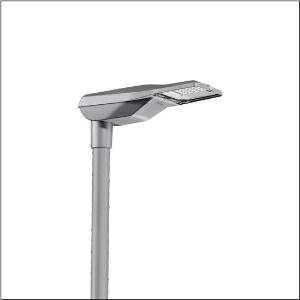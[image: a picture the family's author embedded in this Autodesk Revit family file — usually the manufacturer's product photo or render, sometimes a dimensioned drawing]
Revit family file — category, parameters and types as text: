
# Revit family: streetlight_sl_21_iq_micro___st1_5a_5xe1p41d08db_9421
name_source: partatom
category: Lighting Fixtures
units: mm (PartAtom-declared; Revit-internal decimal feet)

## family parameters
Cut with Voids When Loaded = No
Host = Face
Light Source = No
Part Type = Normal
Room Calculation Point = No
Round Connector Dimension = Use Diameter
Shared = No

## types (1)
- --- (1 x LED, 4930 lm, 36.4 W, 4000K)
    Apparent Load = 36 VA
    CIE Flux Codes = 22 53 95 100 100
    Color Rendering = 70
    Color Temperature = 4000K
    Default Elevation = 1800 mm
    Description = Streetlight SL 21 iQ micro, mast luminaire, primary light control with lens, of PMMA, primary optical cover: cover, of toughened safety glass, transparent, light distribution: ST1.5a, light emission: direct distribution, primary light characteristic: asymmetric, installation type: post-top, side-entry, LED, High Power LED, rated luminous flux: 4.930lm, luminous efficacy: 135lm/W, light colour: 740, colour temperature: 4000K, control: Auto-Match, Temp-Guard, Lumen-Switch, Night-Set, Smart-Wire, Light-Fading, Desk-Remote (wireless, voltage-free reading and setting of iQ features in the workshop via application-optimized NFC function/RFID function), optimised constant luminous flux control (CLO 2.0), presetting dimming linear, mains connection: 220..240V, AC, 50/60Hz, start of lifetime: 36W, end of service life: 38W, reduction: 16W, luminaire housing, of diecast aluminium, powder-coated, Siteco® metallic grey (DB 702S), corrosivity category C5 mid according to DIN EN ISO 12944, please order mast flange separately, inclination adjustable: 0°, 5°, 10°, 15°, sealing non-destructively replaceable, multi-level sealing system, length: 528mm, width: 235mm, height: 110mm, mast flange for spigot size: 42mm (side-entry): 5XC10008XM4, 60/48mm (side-entry/post-top): 5XC10108XM2, 76/60mm (side-entry/post-top): 5XC10108XM1, protection rating (complete): IP66, insulation class (complete): insulation class II (safety insulation), certification: CE, ENEC, ENEC+, VDE, impact resistance: IK09, permissible operating ambient temperature for outdoor applications: -40..+50°C, standard-compliant lighting for roads and squares, packaging unit: 1 piece

Light Distribution: ST1.5a
    Height = 110 mm
    Lamp = 1 x LED
    Lamp Light Flux = 4930 lm
    Lamp Power = 36.4 W
    Lamp count = 1
    Length = 528 mm
    Luminous efficacy = 135 lm/W
    Manufacturer = Siteco
    ModVariant = No
    Model = 5XE1P41D08DB
    Number of Poles = 1
    OnlyDefault = Yes
    Power Factor = 1
    Product Name = Streetlight SL 21 iQ micro | ST1.5a
    Product group = mast luminaire | pylon top
    ProductGroupID = 6100
    Protection Class = Protection class II
    Protection Degree = IP 66
    RLX_Detail_Level = 1
    RLX_Emergency_Light_Flux = 0 lm
    RLX_Emergency_Type = 0
    RLX_Emergency_Type_DB = No
    RlxData = <blob elided: 103145 chars, md5=b4de47a0>
    Socket = socket
    Standby Power = 0 W
    System Light Flux = 4930 lm
    System Power = 36 W
    Type Comments = factory setting: luminous flux: 100 % | dim-lin: 254 | 715 mA
    Type Image = l_1006881.jpg
    URL = http://relux.com
    VarID = @adj_103981
    Voltage = 0 V
    Weight = 0.00 kg
    Width = 235 mm

## geometry (parser evidence)
native form markers: Blend x4, Sweep x11
no freeform markers — native parametric forms only
